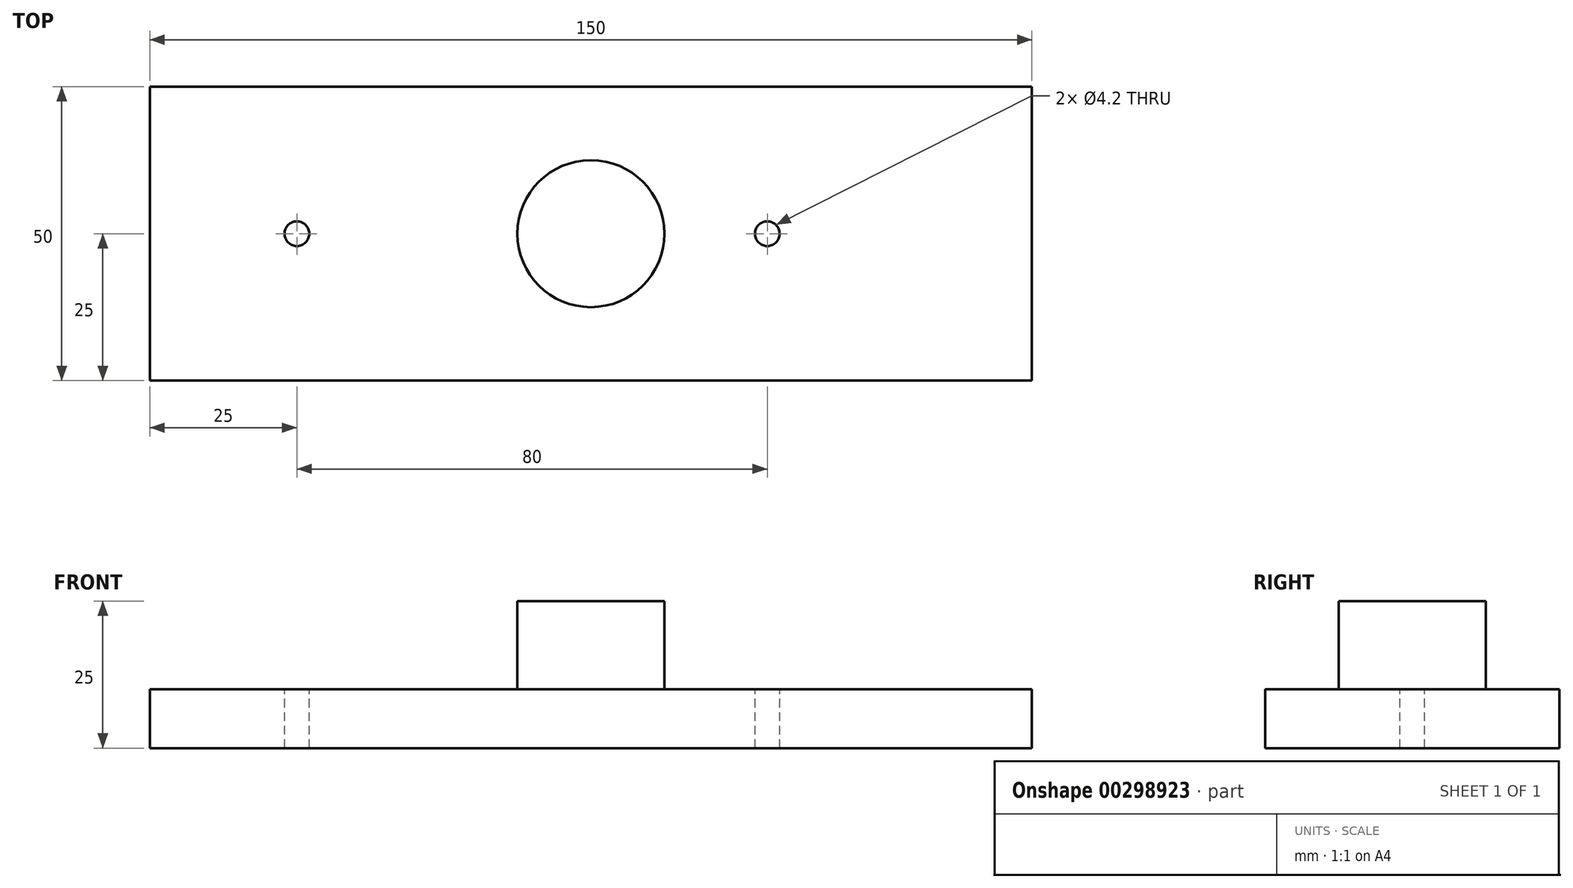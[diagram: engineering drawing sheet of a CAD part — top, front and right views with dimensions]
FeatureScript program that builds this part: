
annotation { "Feature Type Name" : "Feature", "Feature Type Description" : "" }
export const myFeature = defineFeature(function(context is Context, id is Id, definition is map)
    precondition{}
    {
        {
            var Q0;
            Q0=qCreatedBy(makeId("Top.planeOp"),FACE);
            var sketch = newSketch(context, id + "F0", { "sketchPlane" : qUnion([Q0])});
            skLineSegment(sketch, "E0.bottom", {"start": v(-75, 25) * mm, "end": v(75, 25) * mm});
            skLineSegment(sketch, "E0.top", {"start": v(-75, -25) * mm, "end": v(75, -25) * mm});
            skLineSegment(sketch, "E0.left", {"start": v(-75, 25) * mm, "end": v(-75, -25) * mm});
            skLineSegment(sketch, "E0.right", {"start": v(75, 25) * mm, "end": v(75, -25) * mm});
            skPoint(sketch, "E0.middle", {"position": v(0, 0) * mm});
            skSolve(sketch);
        }
        {
            var Q0;
            Q0=makeQuery(id+"F0.imprint","IMPRINT",FACE,{"disambiguationData":[TD([[makeQuery(id+"F0.imprint","IMPRINT",EDGE,{"derivedFrom":sQuery(id+"F0.wireOp",EDGE,"E0.bottom")}),-1.0]])]});
            extrude(context, id + "F1", {"entities" : qUnion([Q0]), "depth" : 10 * mm});
        }
        {
            var Q0;
            Q0=makeQuery(id+"F1.opExtrude","CAP_FACE",FACE,{"disambiguationData":[OSD([sQuery(id+"F0.wireOp",EDGE,"E0.bottom"),sQuery(id+"F0.wireOp",EDGE,"E0.top"),sQuery(id+"F0.wireOp",EDGE,"E0.left"),sQuery(id+"F0.wireOp",EDGE,"E0.right")])],"isStart":false});
            var sketch = newSketch(context, id + "F2", { "sketchPlane" : qUnion([Q0])});
            skCircle(sketch, "E1", {"center": v(0, 0) * mm, "radius": 12.5 * mm});
            skSolve(sketch);
        }
        {
            var Q0;
            Q0 = qSketchRegion(id + "F2", true);
            extrude(context, id + "F3", {"entities" : qUnion([Q0]), "operationType" : NewBodyOperationType.ADD, "depth" : 15 * mm});
        }
        {
            var Q0;
            Q0=makeQuery(id+"F1.opExtrude","CAP_FACE",FACE,{"disambiguationData":[OSD([sQuery(id+"F0.wireOp",EDGE,"E0.bottom"),sQuery(id+"F0.wireOp",EDGE,"E0.top"),sQuery(id+"F0.wireOp",EDGE,"E0.left"),sQuery(id+"F0.wireOp",EDGE,"E0.right")])],"isStart":false});
            var sketch = newSketch(context, id + "F4", { "sketchPlane" : qUnion([Q0])});
            skPoint(sketch, "E2", {"position": v(-50, 0) * mm});
            skPoint(sketch, "E3", {"position": v(30, 0) * mm});
            skSolve(sketch);
        }
        {
            var Q0;
            Q0=sQuery(id+"F4.wireOp",VERTEX,"E2");
            var Q1;
            Q1=sQuery(id+"F4.wireOp",VERTEX,"E3");
            var Q2;
            Q2=makeQuery(id+"F1.opExtrude","SWEPT_BODY",BODY,{"disambiguationData":[OSD([sQuery(id+"F0.wireOp",EDGE,"E0.bottom"),sQuery(id+"F0.wireOp",EDGE,"E0.top"),sQuery(id+"F0.wireOp",EDGE,"E0.left"),sQuery(id+"F0.wireOp",EDGE,"E0.right")])]});
            hole(context, id + "F5", {"style" : HoleStyle.SIMPLE, "endStyle" : HoleEndStyle.THROUGH, "standardTappedOrClearance" : lookupTablePath({ "standard" : "ISO", "engagement" : "75%", "pitch" : "0.8 mm", "size" : "M5", "type" : "Tapped" }), "standardBlindInLast" : lookupTablePath({ "standard" : "ISO", "engagement" : "75%", "pitch" : "0.8 mm", "size" : "M5", "type" : "Tapped" }), "holeDiameter" : 4.2 * mm, "showTappedDepth" : true, "tappedDepth" : 12 * mm, "tapClearance" : 3, "locations" : qUnion([Q0, Q1]), "scope" : qUnion([Q2]), "majorDiameter" : 5 * mm});
        }
    });
